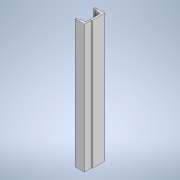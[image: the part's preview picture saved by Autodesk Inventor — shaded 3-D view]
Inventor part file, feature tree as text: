
AUTODESK INVENTOR PART (.ipt)
format: ipt  version: 2020.1 (Build 241239000, 239)  size: 114,688 bytes
history: native  units: mm
features: other x1, extrude x1, sketch x1
ambient origin geometry x8: Origin, YZ Plane, XZ Plane, XY Plane, X Axis, Y Axis, Z Axis, Center Point
bodies: Body1 (feature_tree)
feature tree (3):
  other  "Твердое тело1"
  extrude  "Выдавливание1"  Depth=120.0mm
  sketch  "Эскиз1"
